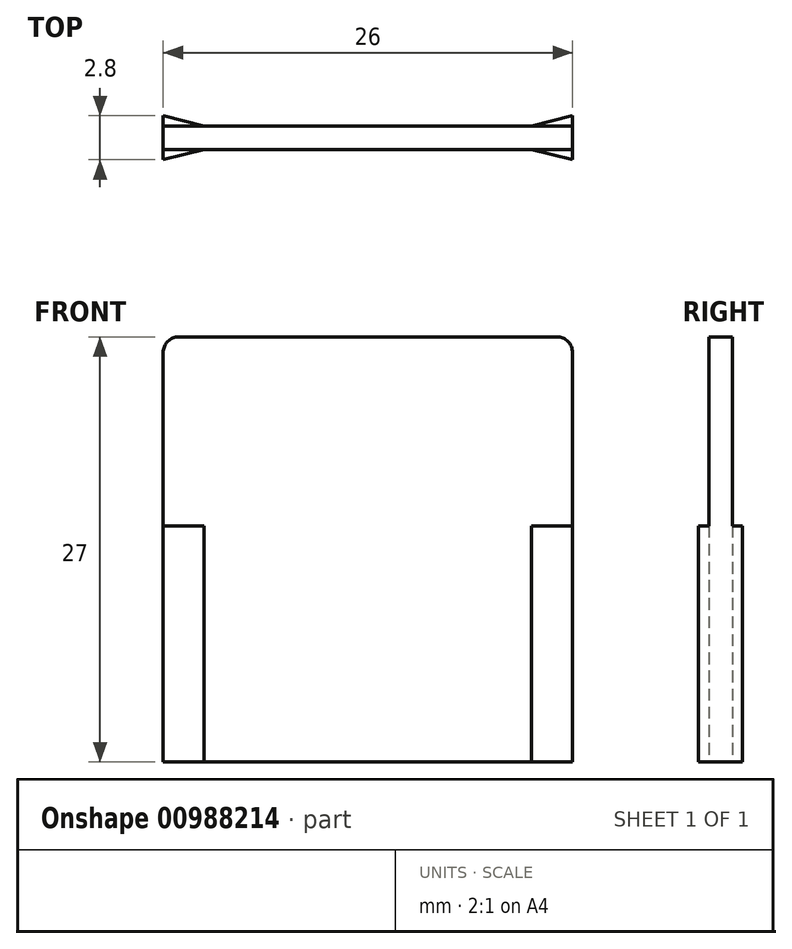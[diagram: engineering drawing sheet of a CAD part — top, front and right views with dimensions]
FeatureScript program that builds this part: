
annotation { "Feature Type Name" : "Feature", "Feature Type Description" : "" }
export const myFeature = defineFeature(function(context is Context, id is Id, definition is map)
    precondition{}
    {
        {
            var Q0;
            Q0=qCreatedBy(makeId("Top.planeOp"),FACE);
            var sketch = newSketch(context, id + "F0", { "sketchPlane" : qUnion([Q0])});
            skLineSegment(sketch, "E0.bottom", {"start": v(-13, 0.75) * mm, "end": v(13, 0.75) * mm});
            skLineSegment(sketch, "E0.top", {"start": v(-13, -0.75) * mm, "end": v(13, -0.75) * mm});
            skLineSegment(sketch, "E0.left", {"start": v(-13, 0.75) * mm, "end": v(-13, -0.75) * mm});
            skLineSegment(sketch, "E0.right", {"start": v(13, 0.75) * mm, "end": v(13, -0.75) * mm});
            skLineSegment(sketch, "E1", {"start": v(-10.4, 0.75) * mm, "end": v(-13, 1.4) * mm});
            skLineSegment(sketch, "E2", {"start": v(-13, 1.4) * mm, "end": v(-13, -1.4) * mm});
            skLineSegment(sketch, "E3", {"start": v(-13, -1.4) * mm, "end": v(-10.4, -0.75) * mm});
            skLineSegment(sketch, "E4.MirrorCS", {"start": v(10.4, 0.75) * mm, "end": v(13, 1.4) * mm});
            skLineSegment(sketch, "E5.MirrorCS", {"start": v(13, 1.4) * mm, "end": v(13, -1.4) * mm});
            skLineSegment(sketch, "E6.MirrorCS", {"start": v(13, -1.4) * mm, "end": v(10.4, -0.75) * mm});
            skSolve(sketch);
        }
        {
            var Q0;
            {var subQ6=sQuery(id+"F0.wireOp",EDGE,"E0.left");Q0=makeQuery(id+"F0.imprint","IMPRINT",FACE,{"disambiguationData":[TD([[makeQuery(id+"F0.imprint","IMPRINT",EDGE,{"derivedFrom":subQ6}),1.0]])]});}
            extrude(context, id + "F1", {"entities" : qUnion([Q0]), "depth" : 27 * mm, "offsetDistance" : 25 * mm});
        }
        {
            var Q0;
            {var subQ0=sQuery(id+"F0.wireOp",EDGE,"E1");Q0=makeQuery(id+"F0.imprint","IMPRINT",FACE,{"disambiguationData":[TD([[makeQuery(id+"F0.imprint","IMPRINT",EDGE,{"derivedFrom":subQ0}),1.0]])]});}
            var Q1;
            {var subQ0=sQuery(id+"F0.wireOp",EDGE,"E3");Q1=makeQuery(id+"F0.imprint","IMPRINT",FACE,{"disambiguationData":[TD([[makeQuery(id+"F0.imprint","IMPRINT",EDGE,{"derivedFrom":subQ0}),1.0]])]});}
            var Q2;
            {var subQ3=sQuery(id+"F0.wireOp",EDGE,"E4.MirrorCS");Q2=makeQuery(id+"F0.imprint","IMPRINT",FACE,{"disambiguationData":[TD([[makeQuery(id+"F0.imprint","IMPRINT",EDGE,{"derivedFrom":subQ3}),-1.0]])]});}
            var Q3;
            {var subQ3=sQuery(id+"F0.wireOp",EDGE,"E6.MirrorCS");Q3=makeQuery(id+"F0.imprint","IMPRINT",FACE,{"disambiguationData":[TD([[makeQuery(id+"F0.imprint","IMPRINT",EDGE,{"derivedFrom":subQ3}),-1.0]])]});}
            extrude(context, id + "F2", {"entities" : qUnion([Q0, Q1, Q2, Q3]), "operationType" : NewBodyOperationType.ADD, "depth" : 15 * mm, "offsetDistance" : 25 * mm});
        }
        {
            var Q0;
            Q0=makeQuery(id+"F1.opExtrude","CAP_EDGE",EDGE,{"disambiguationData":[OSD([sQuery(id+"F0.wireOp",EDGE,"E0.left")])],"isStart":false});
            var Q1;
            Q1=makeQuery(id+"F1.opExtrude","CAP_EDGE",EDGE,{"disambiguationData":[OSD([sQuery(id+"F0.wireOp",EDGE,"E0.right")])],"isStart":false});
            fillet(context, id + "F3", {"entities" : qUnion([Q0, Q1]), "radius" : 1 * mm, "tangentPropagation" : true, "allowEdgeOverflow" : false});
        }
    });
